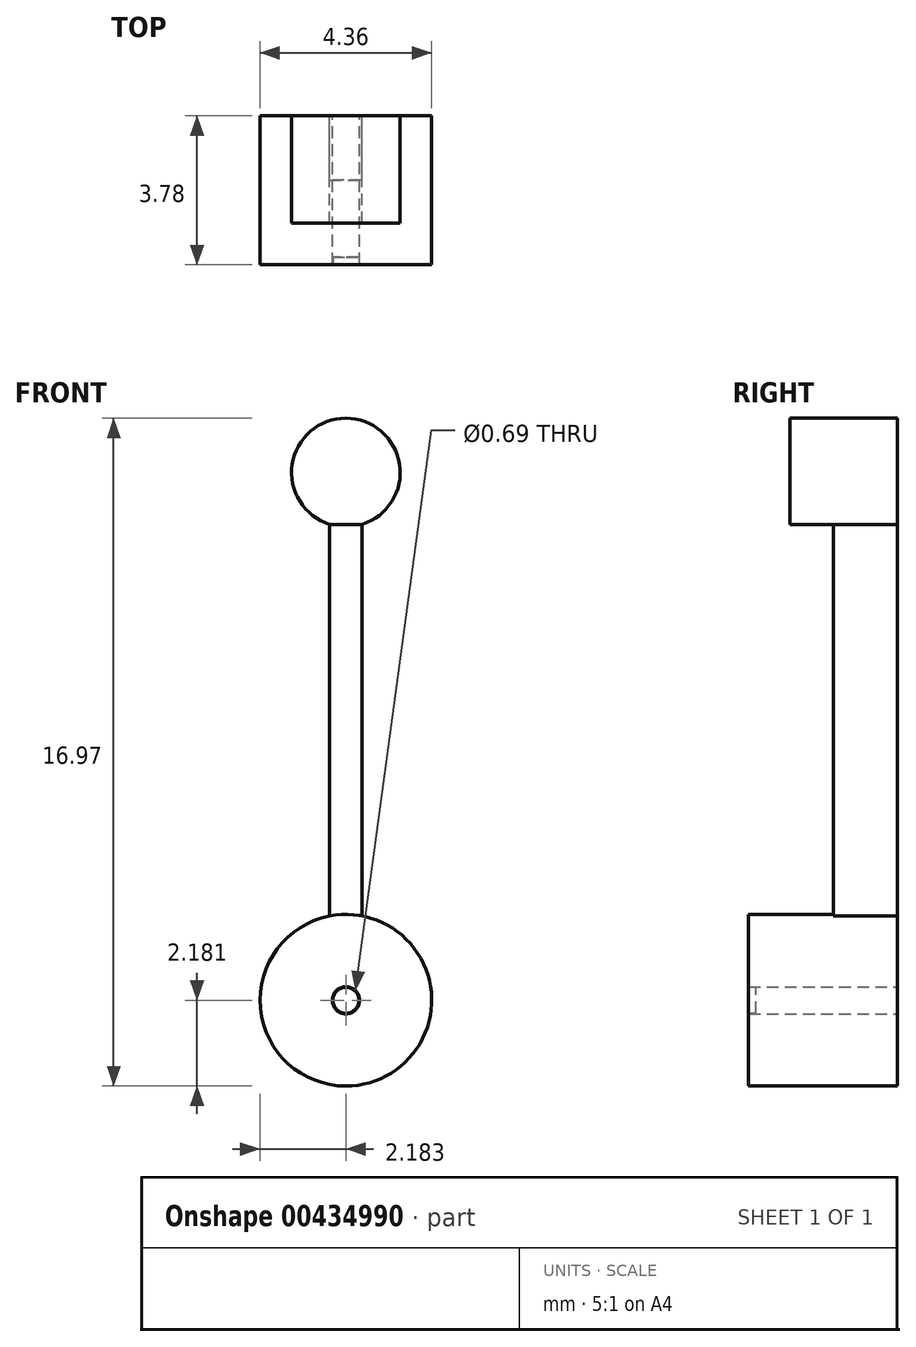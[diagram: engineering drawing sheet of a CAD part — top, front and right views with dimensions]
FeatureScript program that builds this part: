
annotation { "Feature Type Name" : "Feature", "Feature Type Description" : "" }
export const myFeature = defineFeature(function(context is Context, id is Id, definition is map)
    precondition{}
    {
        {
            var Q0;
            Q0=qCreatedBy(makeId("Front.planeOp"),FACE);
            var sketch = newSketch(context, id + "F0", { "sketchPlane" : qUnion([Q0])});
            skCircle(sketch, "E0", {"center": v(-37.57, 7.82) * mm, "radius": 2.18 * mm});
            skCircle(sketch, "E1", {"center": v(-37.57, 7.82) * mm, "radius": 0.34 * mm});
            skLineSegment(sketch, "E2", {"start": v(-37.98, 9.96) * mm, "end": v(-37.98, 19.91) * mm});
            skLineSegment(sketch, "E3", {"start": v(-37.16, 19.91) * mm, "end": v(-37.16, 9.96) * mm});
            skArc(sketch, "E4", {"start": v(-37.16, 19.91) * mm, "mid": v(-37.57, 22.6) * mm, "end": v(-37.98, 19.91) * mm});
            skSolve(sketch);
        }
        {
            var Q0;
            {var subQ0=sQuery(id+"F0.wireOp",EDGE,"E2");Q0=makeQuery(id+"F0.imprint","IMPRINT",FACE,{"disambiguationData":[TD([[makeQuery(id+"F0.imprint","IMPRINT",EDGE,{"derivedFrom":subQ0}),-1.0]])]});}
            var sketch = newSketch(context, id + "F1", { "sketchPlane" : qUnion([Q0])});
            skLineSegment(sketch, "E5", {"start": v(-38.03, 19.91) * mm, "end": v(-37.12, 19.91) * mm});
            skSolve(sketch);
        }
        {
            var Q0;
            Q0=makeQuery(id+"F0.imprint","IMPRINT",FACE,{"disambiguationData":[TD([[makeQuery(id+"F0.imprint","IMPRINT",EDGE,{"derivedFrom":sQuery(id+"F0.wireOp",EDGE,"E1")}),-1.0]])]});
            extrude(context, id + "F2", {"entities" : qUnion([Q0]), "depth" : 1.89 * mm});
        }
        {
            var Q0;
            {var subQ0=sQuery(id+"F1.wireOp",EDGE,"E5");var subQ1=sQuery(id+"F0.wireOp",EDGE,"E2");var subQ2=makeQuery(id+"F0.imprint","IMPRINT",EDGE,{"derivedFrom":subQ1});var subQ3=makeQuery(id+"F1.imprint","INTERSECT",VERTEX,{"derivedFrom":[subQ2,subQ0]});Q0=makeQuery(id+"F1.imprint","IMPRINT",FACE,{"disambiguationData":[TD([[makeQuery(id+"F1.imprint","IMPRINT",EDGE,{"disambiguationData":[TD([[subQ3,-1.0]])],"derivedFrom":subQ0}),-1.0]])]});}
            extrude(context, id + "F3", {"entities" : qUnion([Q0]), "operationType" : NewBodyOperationType.ADD, "depth" : 1.63 * mm});
        }
        {
            var Q0;
            {var subQ5=makeQuery(id+"F0.imprint","IMPRINT",EDGE,{"derivedFrom":sQuery(id+"F0.wireOp",EDGE,"E4")});Q0=makeQuery(id+"F1.imprint","IMPRINT",FACE,{"disambiguationData":[TD([[makeQuery(id+"F1.imprint","IMPRINT",EDGE,{"derivedFrom":subQ5}),1.0]])]});}
            extrude(context, id + "F4", {"entities" : qUnion([Q0]), "operationType" : NewBodyOperationType.ADD, "depth" : 2.73 * mm});
        }
        {
            var Q0;
            Q0=makeQuery(id+"F2.opExtrude","CAP_FACE",FACE,{"disambiguationData":[OSD([sQuery(id+"F0.wireOp",EDGE,"E0"),sQuery(id+"F0.wireOp",EDGE,"E1")])],"isStart":false});
            extrude(context, id + "F5", {"entities" : qUnion([Q0]), "operationType" : NewBodyOperationType.ADD, "depth" : 1.89 * mm});
        }
        {
            var Q0;
            Q0=makeQuery(id+"F5.opExtrude","CAP_FACE",FACE,{"disambiguationData":[OSD([sQuery(id+"F0.wireOp",EDGE,"E0"),sQuery(id+"F0.wireOp",EDGE,"E1")])],"isStart":false});
            var sketch = newSketch(context, id + "F6", { "sketchPlane" : qUnion([Q0])});
            skCircle(sketch, "E6", {"center": v(-37.57, 7.82) * mm, "radius": 0.33 * mm});
            skSolve(sketch);
        }
        {
            var Q0;
            Q0 = qSketchRegion(id + "F6", true);
            extrude(context, id + "F7", {"entities" : qUnion([Q0]), "oppositeDirection" : true, "depth" : 0.19 * mm});
        }
    });
